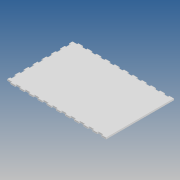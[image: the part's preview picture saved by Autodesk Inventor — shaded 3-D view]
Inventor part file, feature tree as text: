
AUTODESK INVENTOR PART (.ipt)
format: ipt  version: 2020 (Build 240168000, 168)  size: 185,856 bytes
history: native  units: mm
features: extrude x3, sketch x3, pattern_linear x2, mirror x1
ambient origin geometry x8: Origin, YZ Plane, XZ Plane, XY Plane, X Axis, Y Axis, Z Axis, Center Point
bodies: Body1 (feature_tree)
feature tree (9):
  extrude  "Выдавливание5"  Depth=220.0mm
  extrude  "Выдавливание6"  Depth=149.0mm
  pattern_linear  "Прямоуг.массив6"  Spacing1=3.0mm  [1 undecoded]
  extrude  "Выдавливание8"  Depth=3.0mm
  pattern_linear  "Прямоуг.массив7"  Spacing1=10.0mm  [1 undecoded]
  mirror  "Зеркальное отражение2"
  sketch  "Эскиз5"
  sketch  "Эскиз6"
  sketch  "Эскиз8"
note: 2 required parameter values undecoded (feature->parameter linkage not recoverable at this tier; creation-order binding heuristic only, values carry confidence <= 0.55)
